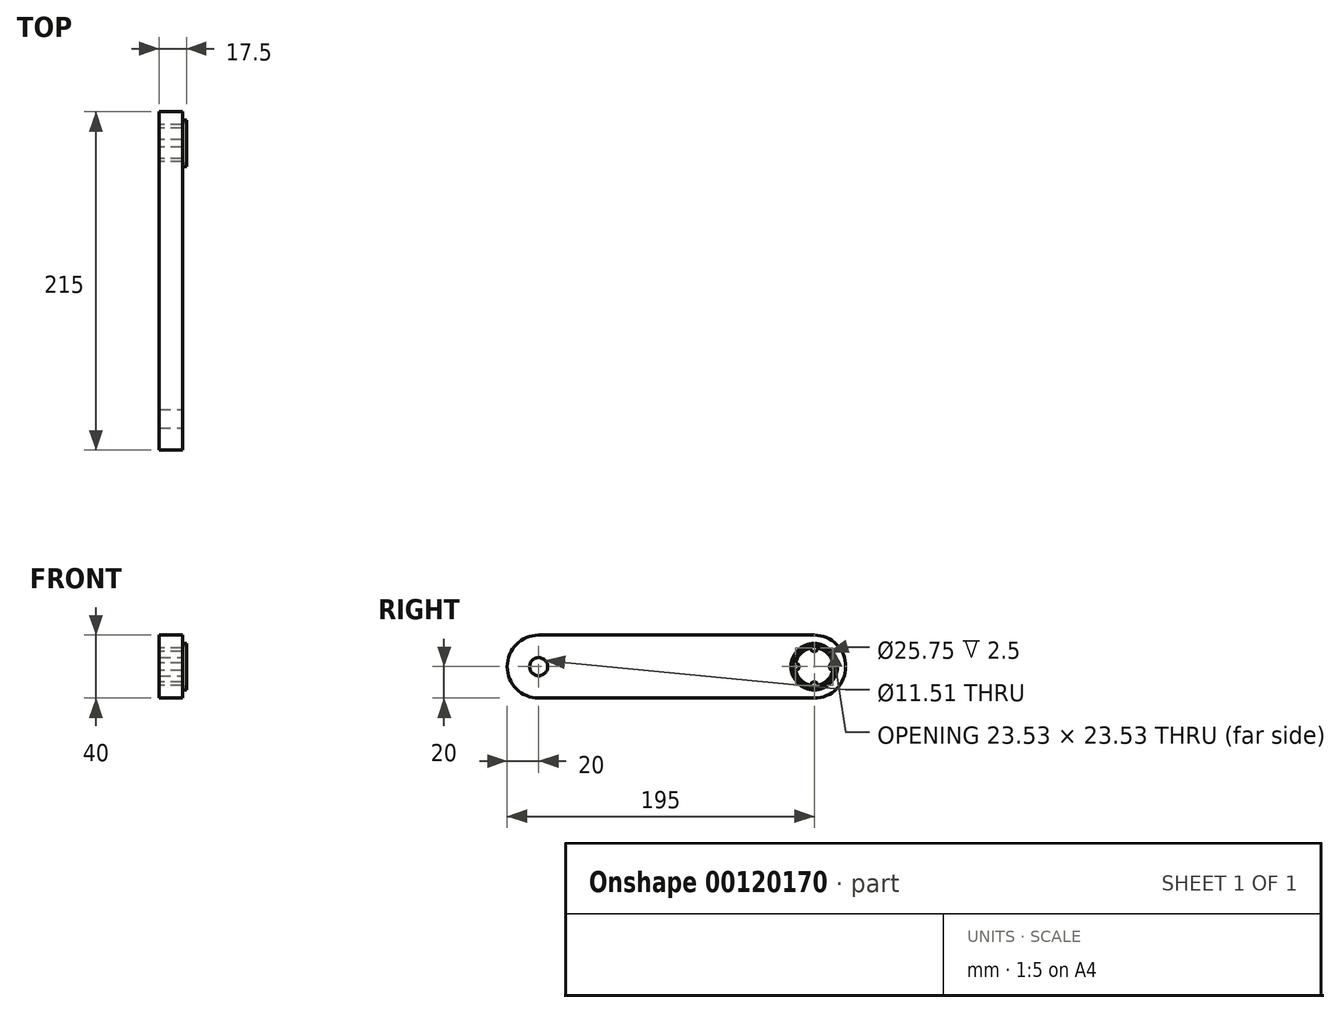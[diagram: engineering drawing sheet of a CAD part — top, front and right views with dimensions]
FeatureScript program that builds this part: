
annotation { "Feature Type Name" : "Feature", "Feature Type Description" : "" }
export const myFeature = defineFeature(function(context is Context, id is Id, definition is map)
    precondition{}
    {
        {
            var Q0;
            Q0=qCreatedBy(makeId("Right.planeOp"),FACE);
            var sketch = newSketch(context, id + "F0", { "sketchPlane" : qUnion([Q0])});
            skArc(sketch, "E0", {"start": v(0, -20) * mm, "mid": v(20, 0) * mm, "end": v(0, 20) * mm});
            skArc(sketch, "E1", {"start": v(-175, 20) * mm, "mid": v(-195, 0) * mm, "end": v(-175, -20) * mm});
            skLineSegment(sketch, "E2", {"start": v(-175, 20) * mm, "end": v(0, 20) * mm});
            skLineSegment(sketch, "E3", {"start": v(-175, -20) * mm, "end": v(0, -20) * mm});
            skArc(sketch, "E4", {"start": v(-2.37, 11.76) * mm, "mid": v(-8.49, 8.49) * mm, "end": v(-11.76, 2.37) * mm});
            skArc(sketch, "E5", {"start": v(-2.37, 11.76) * mm, "mid": v(0, 9.62) * mm, "end": v(2.37, 11.76) * mm});
            skArc(sketch, "E6", {"start": v(11.76, 2.37) * mm, "mid": v(9.62, 0) * mm, "end": v(11.76, -2.37) * mm});
            skArc(sketch, "E7", {"start": v(2.37, -11.76) * mm, "mid": v(0, -9.62) * mm, "end": v(-2.37, -11.76) * mm});
            skArc(sketch, "E8", {"start": v(-11.76, -2.37) * mm, "mid": v(-9.62, 0) * mm, "end": v(-11.76, 2.37) * mm});
            skArc(sketch, "E9.trimOffspring", {"start": v(11.76, 2.37) * mm, "mid": v(8.49, 8.49) * mm, "end": v(2.37, 11.76) * mm});
            skArc(sketch, "E10.trimOffspring", {"start": v(2.37, -11.76) * mm, "mid": v(8.49, -8.49) * mm, "end": v(11.76, -2.37) * mm});
            skArc(sketch, "E11.trimOffspring", {"start": v(-11.76, -2.37) * mm, "mid": v(-8.49, -8.49) * mm, "end": v(-2.37, -11.76) * mm});
            skLineSegment(sketch, "E12", {"start": v(-87.5, 20) * mm, "end": v(-87.5, -20) * mm, "construction": true});
            skSolve(sketch);
        }
        {
            var Q0;
            Q0 = qSketchRegion(id + "F0", true);
            extrude(context, id + "F1", {"entities" : qUnion([Q0]), "depth" : 15 * mm});
        }
        {
            var Q0;
            Q0=makeQuery(id+"F1.opExtrude","CAP_FACE",FACE,{"disambiguationData":[OSD([sQuery(id+"F0.wireOp",EDGE,"E0"),sQuery(id+"F0.wireOp",EDGE,"E1"),sQuery(id+"F0.wireOp",EDGE,"E2"),sQuery(id+"F0.wireOp",EDGE,"E3"),sQuery(id+"F0.wireOp",EDGE,"E4"),sQuery(id+"F0.wireOp",EDGE,"E5"),sQuery(id+"F0.wireOp",EDGE,"E6"),sQuery(id+"F0.wireOp",EDGE,"E7"),sQuery(id+"F0.wireOp",EDGE,"E8"),sQuery(id+"F0.wireOp",EDGE,"E9.trimOffspring"),sQuery(id+"F0.wireOp",EDGE,"E10.trimOffspring"),sQuery(id+"F0.wireOp",EDGE,"E11.trimOffspring"),sQuery(id+"F0.wireOp",EDGE,"ee303826-bd56-40a6-9684-36cbc93daedd0.MirrorCS"),sQuery(id+"F0.wireOp",EDGE,"45451ff8-182d-48c6-bf7a-9b6e788b30d50.MirrorCS"),sQuery(id+"F0.wireOp",EDGE,"36f576d3-0dba-486c-b78c-9017242475770.MirrorCS"),sQuery(id+"F0.wireOp",EDGE,"045a34b7-e9a3-4159-9caa-920cca6acea20.MirrorCS"),sQuery(id+"F0.wireOp",EDGE,"a170af7f-84ef-4543-8da2-f3df5b5d89da0.MirrorCS"),sQuery(id+"F0.wireOp",EDGE,"0cfc4451-a1fb-49c8-9f1c-4c833e65308b0.MirrorCS"),sQuery(id+"F0.wireOp",EDGE,"1424cbeb-20e6-4b5a-ac30-f8d93b52161b0.MirrorCS"),sQuery(id+"F0.wireOp",EDGE,"814a3db4-c2fb-4b6c-8bc0-233ecbe1cfcc0.MirrorCS")])],"isStart":false});
            var sketch = newSketch(context, id + "F2", { "sketchPlane" : qUnion([Q0])});
            skCircle(sketch, "E13", {"center": v(0, 0) * mm, "radius": 14.76 * mm});
            skCircle(sketch, "E14", {"center": v(0, 0) * mm, "radius": 12.88 * mm});
            skSolve(sketch);
        }
        {
            var Q0;
            Q0 = qSketchRegion(id + "F2", true);
            extrude(context, id + "F3", {"entities" : qUnion([Q0]), "operationType" : NewBodyOperationType.ADD, "depth" : 2.5 * mm});
        }
        {
            var Q0;
            {var subQ0=sQuery(id+"F0.wireOp",EDGE,"E3");var subQ1=sQuery(id+"F0.wireOp",EDGE,"E2");var subQ2=sQuery(id+"F0.wireOp",EDGE,"E1");var subQ3=sQuery(id+"F0.wireOp",EDGE,"E0");Q0=makeQuery(id+"F3.boolean.opBoolean","SPLIT",FACE,{"disambiguationData":[TD([makeQuery(id+"F1.opExtrude","SWEPT_FACE",FACE,{"disambiguationData":[OSD([subQ3])]})])],"derivedFrom":makeQuery(id+"F1.opExtrude","CAP_FACE",FACE,{"disambiguationData":[OSD([subQ3,subQ2,subQ1,subQ0,sQuery(id+"F0.wireOp",EDGE,"E4"),sQuery(id+"F0.wireOp",EDGE,"E5"),sQuery(id+"F0.wireOp",EDGE,"E6"),sQuery(id+"F0.wireOp",EDGE,"E7"),sQuery(id+"F0.wireOp",EDGE,"E8"),sQuery(id+"F0.wireOp",EDGE,"E9.trimOffspring"),sQuery(id+"F0.wireOp",EDGE,"E10.trimOffspring"),sQuery(id+"F0.wireOp",EDGE,"E11.trimOffspring")])],"isStart":false})});}
            var sketch = newSketch(context, id + "F4", { "sketchPlane" : qUnion([Q0])});
            skPoint(sketch, "E15", {"position": v(-175, 0) * mm});
            skSolve(sketch);
        }
        {
            var Q0;
            Q0=sQuery(id+"F4.wireOp",VERTEX,"E15");
            var Q1;
            Q1=makeQuery(id+"F1.opExtrude","SWEPT_BODY",BODY,{"disambiguationData":[OSD([sQuery(id+"F0.wireOp",EDGE,"E0"),sQuery(id+"F0.wireOp",EDGE,"E1"),sQuery(id+"F0.wireOp",EDGE,"E2"),sQuery(id+"F0.wireOp",EDGE,"E3"),sQuery(id+"F0.wireOp",EDGE,"E4"),sQuery(id+"F0.wireOp",EDGE,"E5"),sQuery(id+"F0.wireOp",EDGE,"E6"),sQuery(id+"F0.wireOp",EDGE,"E7"),sQuery(id+"F0.wireOp",EDGE,"E8"),sQuery(id+"F0.wireOp",EDGE,"E9.trimOffspring"),sQuery(id+"F0.wireOp",EDGE,"E10.trimOffspring"),sQuery(id+"F0.wireOp",EDGE,"E11.trimOffspring")])]});
            hole(context, id + "F5", {"style" : HoleStyle.SIMPLE, "endStyle" : HoleEndStyle.THROUGH, "standardTappedOrClearance" : lookupTablePath({ "standard" : "ANSI", "engagement" : "75%", "pitch" : "20 tpi", "size" : "1/2", "type" : "Tapped" }), "standardBlindInLast" : lookupTablePath({ "standard" : "ANSI", "engagement" : "75%", "pitch" : "20 tpi", "size" : "1/2", "type" : "Tapped" }), "holeDiameter" : 11.5 * mm, "startFromSketch" : true, "locations" : qUnion([Q0]), "scope" : qUnion([Q1]), "isTappedThrough" : true, "majorDiameter" : 12.7 * mm, "showTappedDepth" : true});
        }
    });
